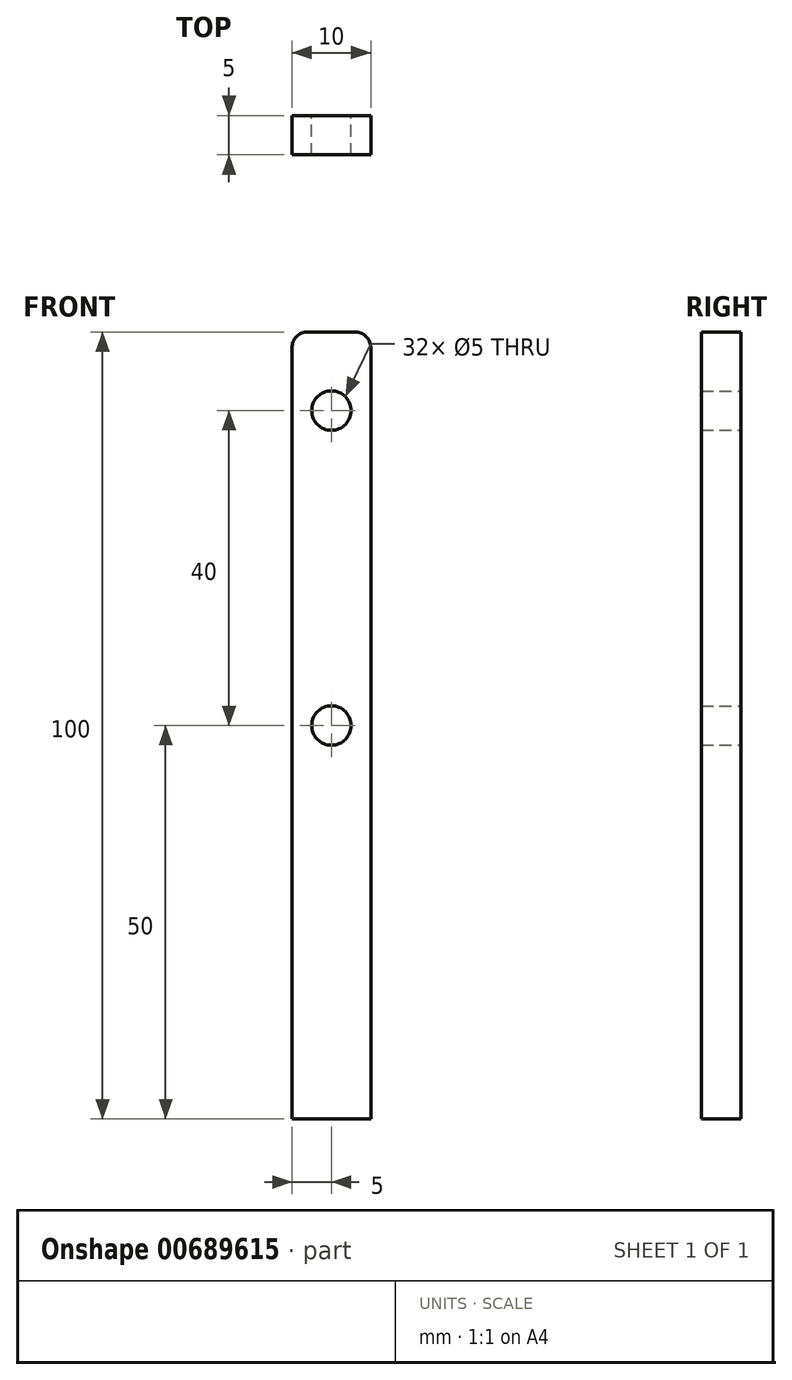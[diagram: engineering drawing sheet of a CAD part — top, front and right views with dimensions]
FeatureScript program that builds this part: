
annotation { "Feature Type Name" : "Feature", "Feature Type Description" : "" }
export const myFeature = defineFeature(function(context is Context, id is Id, definition is map)
    precondition{}
    {
        {
            var Q0;
            Q0=qCreatedBy(makeId("Front.planeOp"),FACE);
            var sketch = newSketch(context, id + "F0", { "sketchPlane" : qUnion([Q0])});
            skLineSegment(sketch, "E0", {"start": v(0, 0) * mm, "end": v(10, 0) * mm});
            skLineSegment(sketch, "E1", {"start": v(10, 0) * mm, "end": v(10, 98) * mm});
            skLineSegment(sketch, "E2", {"start": v(8, 100) * mm, "end": v(2, 100) * mm});
            skLineSegment(sketch, "E3", {"start": v(0, 98) * mm, "end": v(0, 0) * mm});
            skPoint(sketch, "E4.visualSharp", {"position": v(0, 100) * mm});
            skArc(sketch, "E4.filletArc", {"start": v(2, 100) * mm, "mid": v(0.59, 99.41) * mm, "end": v(0, 98) * mm});
            skPoint(sketch, "E5.visualSharp", {"position": v(10, 100) * mm});
            skArc(sketch, "E5.filletArc", {"start": v(10, 98) * mm, "mid": v(9.41, 99.41) * mm, "end": v(8, 100) * mm});
            skSolve(sketch);
        }
        {
            var Q0;
            Q0=makeQuery(id+"F0.imprint","IMPRINT",FACE,{"disambiguationData":[TD([[makeQuery(id+"F0.imprint","IMPRINT",EDGE,{"derivedFrom":sQuery(id+"F0.wireOp",EDGE,"E0")}),1.0]])]});
            extrude(context, id + "F1", {"entities" : qUnion([Q0]), "depth" : 5 * mm, "offsetDistance" : 25 * mm});
        }
        {
            var Q0;
            Q0=qCreatedBy(makeId("Front.planeOp"),FACE);
            var sketch = newSketch(context, id + "F2", { "sketchPlane" : qUnion([Q0])});
            skCircle(sketch, "E6", {"center": v(5, 50) * mm, "radius": 2.5 * mm});
            skCircle(sketch, "E7", {"center": v(5, 90) * mm, "radius": 2.5 * mm});
            skSolve(sketch);
        }
        {
            var Q0;
            Q0=makeQuery(id+"F2.imprint","IMPRINT",FACE,{"disambiguationData":[TD([[makeQuery(id+"F2.imprint","IMPRINT",EDGE,{"derivedFrom":sQuery(id+"F2.wireOp",EDGE,"E7")}),1.0]])]});
            var Q1;
            Q1=makeQuery(id+"F2.imprint","IMPRINT",FACE,{"disambiguationData":[TD([[makeQuery(id+"F2.imprint","IMPRINT",EDGE,{"derivedFrom":sQuery(id+"F2.wireOp",EDGE,"E6")}),1.0]])]});
            extrude(context, id + "F3", {"entities" : qUnion([Q0, Q1]), "operationType" : NewBodyOperationType.REMOVE, "depth" : 5 * mm, "offsetDistance" : 25 * mm});
        }
    });
